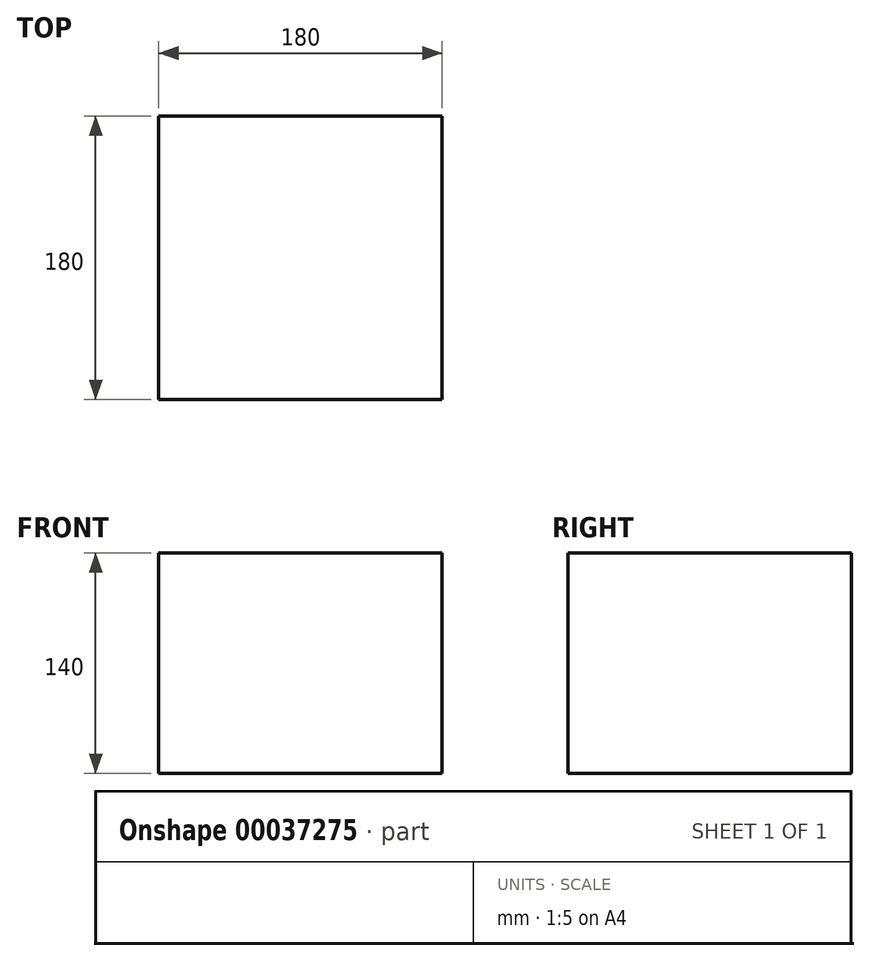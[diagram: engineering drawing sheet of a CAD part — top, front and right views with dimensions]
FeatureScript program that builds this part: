
annotation { "Feature Type Name" : "Feature", "Feature Type Description" : "" }
export const myFeature = defineFeature(function(context is Context, id is Id, definition is map)
    precondition{}
    {
        {
            var Q0;
            Q0=qCreatedBy(makeId("Top.planeOp"),FACE);
            var sketch = newSketch(context, id + "F0", { "sketchPlane" : qUnion([Q0])});
            skLineSegment(sketch, "E0.rect.bottom", {"start": v(90, -90) * mm, "end": v(-90, -90) * mm});
            skLineSegment(sketch, "E0.rect.top", {"start": v(90, 90) * mm, "end": v(-90, 90) * mm});
            skLineSegment(sketch, "E0.rect.left", {"start": v(90, -90) * mm, "end": v(90, 90) * mm});
            skLineSegment(sketch, "E0.rect.right", {"start": v(-90, -90) * mm, "end": v(-90, 90) * mm});
            skPoint(sketch, "E0.rect.middle", {"position": v(0, 0) * mm});
            skSolve(sketch);
        }
        {
            var Q0;
            Q0=makeQuery(id+"F0.imprint","IMPRINT",FACE,{"disambiguationData":[TD([[makeQuery(id+"F0.imprint","IMPRINT",EDGE,{"derivedFrom":sQuery(id+"F0.wireOp",EDGE,"E0.rect.bottom")}),-1.0]])]});
            extrude(context, id + "F1", {"entities" : qUnion([Q0]), "depth" : 140 * mm});
        }
    });
